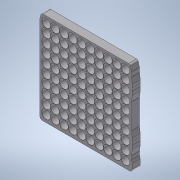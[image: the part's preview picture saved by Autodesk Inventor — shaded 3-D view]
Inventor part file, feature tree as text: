
AUTODESK INVENTOR PART (.ipt)
format: ipt  version: 2020.3 (Build 243373000, 373)  size: 737,280 bytes
history: native  units: in
note: dims shown in document units (in); Inventor stores cm internally (conversion verified against a paired STEP export)
features: pattern_linear x8, fillet x7, sketch x6, extrude x5, hole x4, chamfer x2, plane x1, projected_geometry x1
ambient origin geometry x8: Origin, YZ Plane, XZ Plane, XY Plane, X Axis, Y Axis, Z Axis, Center Point
bodies: Solid1 (feature_tree)
feature tree (34):
  extrude  "Extrusion1"  Depth=5.085in
  hole  "Hole1"  [1 undecoded]
  hole  "Hole7"  [1 undecoded]
  pattern_linear  "Rectangular Pattern1"  Spacing1=0.75in  [1 undecoded]
  pattern_linear  "Rectangular Pattern6"  Spacing1=0.25in  [1 undecoded]
  extrude  "Extrusion8"  Depth=0.375in
  extrude  "Extrusion11"  Depth=0.375in
  fillet  "Fillet9"  Radius=2.075in
  fillet  "Fillet2"  Radius=0.75in
  chamfer  "Chamfer7"  Distance=0.15in
  chamfer  "Chamfer9"  Distance=1.25in
  fillet  "Fillet5"  Radius=5.9in
  pattern_linear  "Rectangular Pattern4"  Spacing1=5.9in  [1 undecoded]
  extrude  "Extrusion9"  Depth=0.375in
  fillet  "Fillet10"  Radius=5.9in
  plane  "Work Plane1"
  hole  "Hole6"  [1 undecoded]
  extrude  "Extrusion12"  Depth=0.375in
  pattern_linear  "Rectangular Pattern5"  Spacing1=0.0515in  [1 undecoded]
  fillet  "Fillet11"  Radius=0.5in
  sketch  "Sketch16"  dims[d50=0.375in]
  hole  "Hole8"  [1 undecoded]
  pattern_linear  "Rectangular Pattern7"  Count1=2 Spacing1=6.0in
  pattern_linear  "Rectangular Pattern8"  Spacing1=0.1in  [1 undecoded]
  pattern_linear  "Rectangular Pattern9"  Spacing1=1.0in  [1 undecoded]
  pattern_linear  "Rectangular Pattern10"  Spacing1=15.0deg  [1 undecoded]
  fillet  "Fillet12"  Radius=1.0in
  fillet  "Fillet13"  Radius=0.5in
  sketch  "Sketch5"  dims[d0=5.085in d1=5.085in]
  sketch  "Sketch11"  dims[d4=1.02in d5=0.0in]
  sketch  "Sketch14"  dims[d6=1.105in d7=0.75in d8=1.146in d9=0.1in d10=0.5635in d11=1.0in d12=0.8108in d13=3.937in d15=1.13in d16=3.937in d18=1.13in]
  projected_geometry  "Projected Loop4"
  sketch  "Sketch15"  dims[d23=6.0in d36=4.52in]
  sketch  "Sketch17"  dims[d63=11.5in d84=0.75in d85=0.125in d86=15.0deg d87=0.25in d89=1.25in d91=3.2in d105=2.075in d109=0.75in d110=0.125in d111=15.0deg d124=0.15in d126=1.25in d128=0.097in d129=0.236in d130=0.375in d131=0.25in d132=0.5635in d133=0.75in d134=0.8108in d135=5.9in d136=5.9in d138=6.0in d146=5.9in d147=0.1in d148=0.0515in d149=0.0515in d151=0.5in d152=1.0in d153=0.0in d154=0.5in d155=0.7874in d157=6.0in d159=0.1in d160=1.0in d161=15.0deg d162=1.0in d163=0.0in d164=0.5in d165=0.1in d170=1.136in d171=0.635in d172=1.0in d173=0.0in d175=0.25in d177=3.39in d178=1.13in d179=1.13in d180=0.4in d181=0.34in d182=0.0in d183=1.1811in d185=1.13in d186=-0.68in d187=0.125in d188=0.128in d189=0.315in d190=0.375in d191=0.25in d192=0.5635in d193=0.465in d194=0.8108in d195=1.9685in d197=2.26in d198=1.9685in d200=2.26in d201=1.109in d202=1.109in d203=1.105in d205=0.025in d206=0.565in d207=0.565in d208=0.128in d209=0.128in d210=0.0481in d211=0.098in d212=0.75in d213=0.375in d214=0.25in d215=0.5635in d216=0.4in d217=0.8108in d218=4.3307in d220=1.13in d221=4.3307in d223=1.13in d224=0.7874in d226=11.3in d227=0.7874in d229=11.3in d230=0.24in d231=0.1in d232=0.375in]
note: 11 required parameter values undecoded (feature->parameter linkage not recoverable at this tier; creation-order binding heuristic only, values carry confidence <= 0.55)
